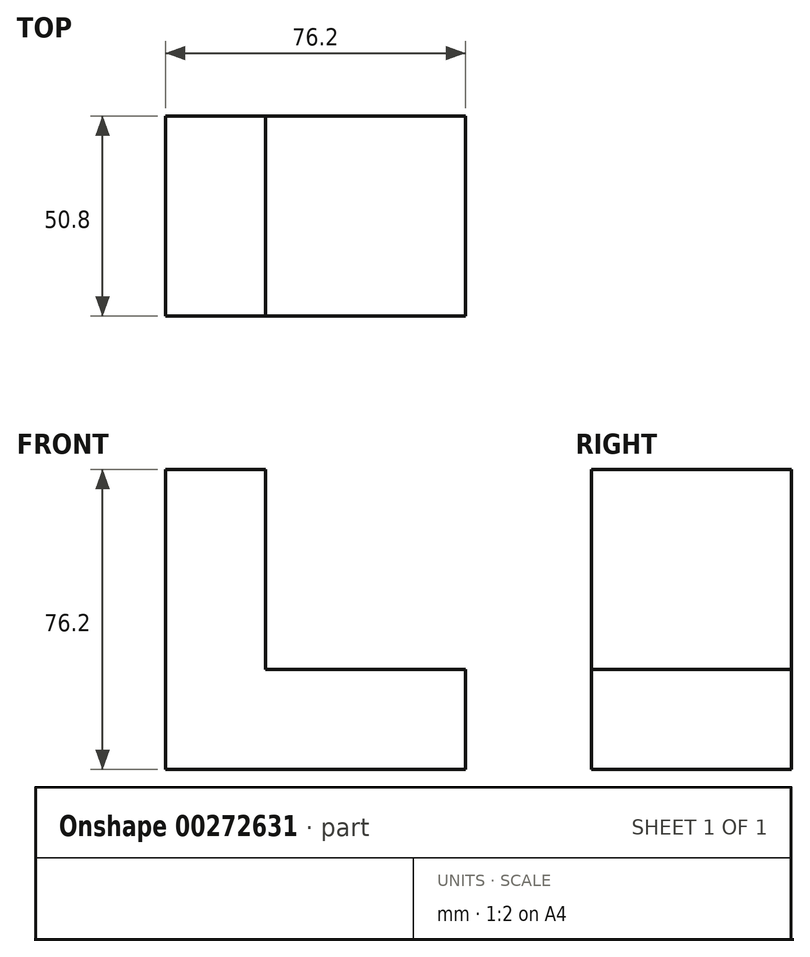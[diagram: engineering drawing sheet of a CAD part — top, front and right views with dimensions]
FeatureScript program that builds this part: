
annotation { "Feature Type Name" : "Feature", "Feature Type Description" : "" }
export const myFeature = defineFeature(function(context is Context, id is Id, definition is map)
    precondition{}
    {
        {
            var Q0;
            Q0=qCreatedBy(makeId("Front.planeOp"),FACE);
            var sketch = newSketch(context, id + "F0", { "sketchPlane" : qUnion([Q0])});
            skLineSegment(sketch, "E0", {"start": v(-25.4, 53.86) * mm, "end": v(0, 53.86) * mm});
            skLineSegment(sketch, "E1", {"start": v(0, 53.86) * mm, "end": v(0, 3.06) * mm});
            skLineSegment(sketch, "E2", {"start": v(0, 3.06) * mm, "end": v(50.8, 3.06) * mm});
            skLineSegment(sketch, "E3", {"start": v(50.8, 3.06) * mm, "end": v(50.8, -22.34) * mm});
            skLineSegment(sketch, "E4", {"start": v(50.8, -22.34) * mm, "end": v(-25.4, -22.34) * mm});
            skLineSegment(sketch, "E5", {"start": v(-25.4, 53.86) * mm, "end": v(-25.4, -22.34) * mm});
            skSolve(sketch);
        }
        {
            var Q0;
            Q0 = qSketchRegion(id + "F0", true);
            extrude(context, id + "F1", {"entities" : qUnion([Q0]), "depth" : 50.8 * mm});
        }
    });
